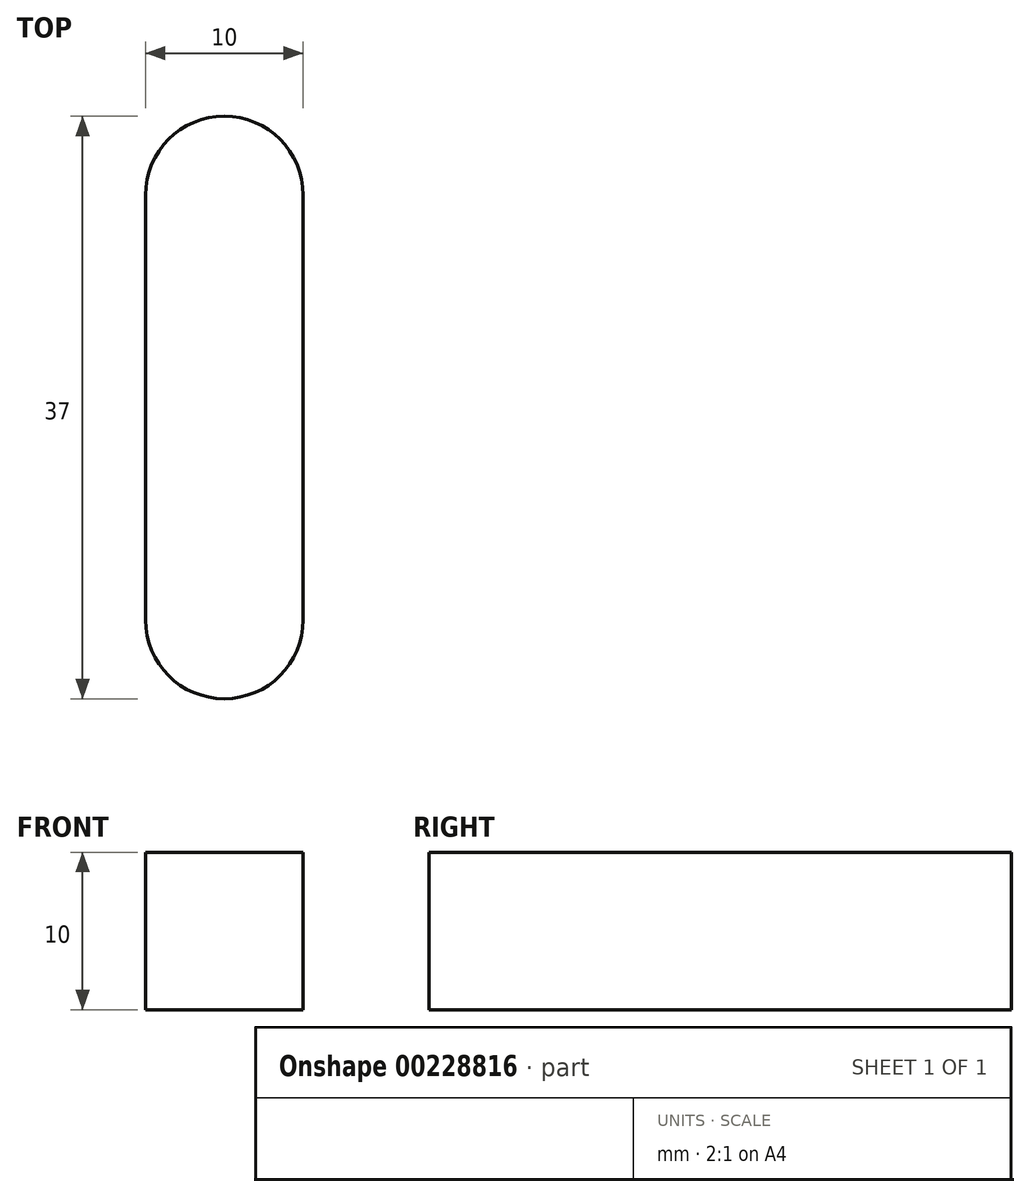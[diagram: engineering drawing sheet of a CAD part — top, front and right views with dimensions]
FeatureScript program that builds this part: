
annotation { "Feature Type Name" : "Feature", "Feature Type Description" : "" }
export const myFeature = defineFeature(function(context is Context, id is Id, definition is map)
    precondition{}
    {
        {
            var Q0;
            Q0=qCreatedBy(makeId("Top.planeOp"),FACE);
            var sketch = newSketch(context, id + "F0", { "sketchPlane" : qUnion([Q0])});
            skLineSegment(sketch, "E0.bottom", {"start": v(-5, 18.5) * mm, "end": v(5, 18.5) * mm});
            skLineSegment(sketch, "E0.top", {"start": v(-5, -18.5) * mm, "end": v(5, -18.5) * mm});
            skLineSegment(sketch, "E0.left", {"start": v(-5, 18.5) * mm, "end": v(-5, -18.5) * mm});
            skLineSegment(sketch, "E0.right", {"start": v(5, 18.5) * mm, "end": v(5, -18.5) * mm});
            skSolve(sketch);
        }
        {
            var Q0;
            Q0=makeQuery(id+"F0.imprint","IMPRINT",FACE,{"disambiguationData":[TD([[makeQuery(id+"F0.imprint","IMPRINT",EDGE,{"derivedFrom":sQuery(id+"F0.wireOp",EDGE,"E0.bottom")}),-1.0]])]});
            extrude(context, id + "F1", {"entities" : qUnion([Q0]), "depth" : 10 * mm});
        }
        {
            var Q0;
            Q0=makeQuery(id+"F1.opExtrude","SWEPT_EDGE",EDGE,{"disambiguationData":[OSD([sQuery(id+"F0.wireOp",EDGE,"E0.bottom"),sQuery(id+"F0.wireOp",EDGE,"E0.left")])]});
            var Q1;
            Q1=makeQuery(id+"F1.opExtrude","SWEPT_EDGE",EDGE,{"disambiguationData":[OSD([sQuery(id+"F0.wireOp",EDGE,"E0.bottom"),sQuery(id+"F0.wireOp",EDGE,"E0.right")])]});
            var Q2;
            Q2=makeQuery(id+"F1.opExtrude","SWEPT_EDGE",EDGE,{"disambiguationData":[OSD([sQuery(id+"F0.wireOp",EDGE,"E0.top"),sQuery(id+"F0.wireOp",EDGE,"E0.left")])]});
            var Q3;
            Q3=makeQuery(id+"F1.opExtrude","SWEPT_EDGE",EDGE,{"disambiguationData":[OSD([sQuery(id+"F0.wireOp",EDGE,"E0.top"),sQuery(id+"F0.wireOp",EDGE,"E0.right")])]});
            fillet(context, id + "F2", {"entities" : qUnion([Q0, Q1, Q2, Q3]), "radius" : 5 * mm, "tangentPropagation" : true, "allowEdgeOverflow" : false});
        }
    });
